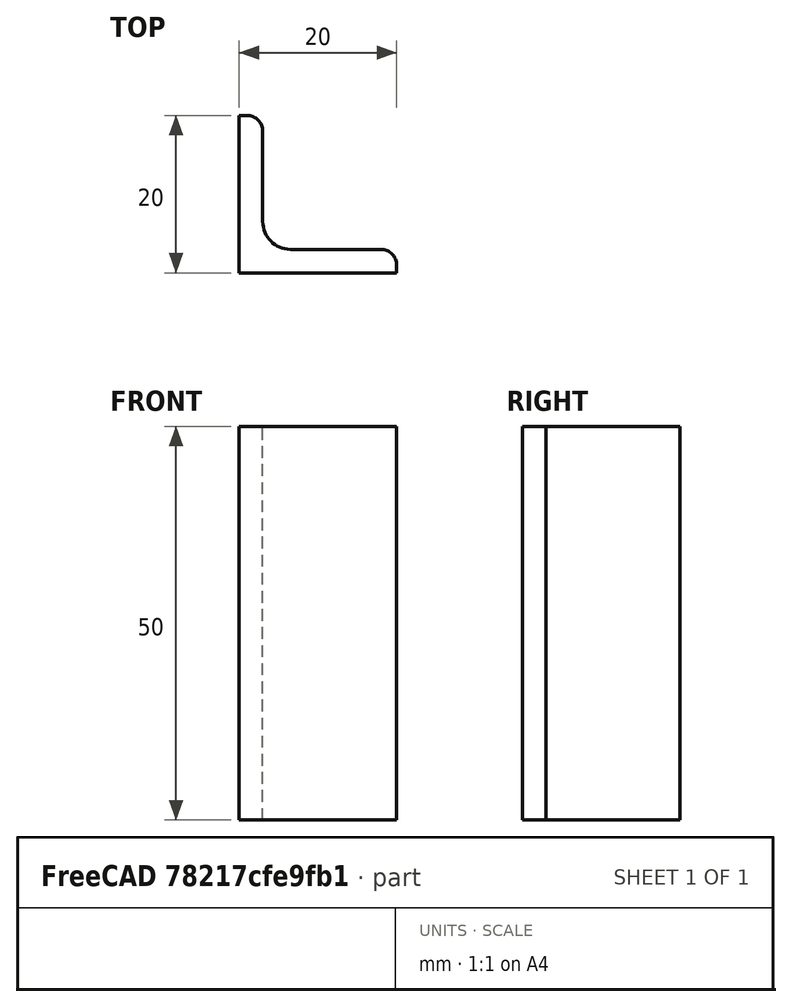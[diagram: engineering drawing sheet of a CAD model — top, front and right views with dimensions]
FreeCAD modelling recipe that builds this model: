
FCSTD DOCUMENT  (FreeCAD 0.15R4671 (Git))
Label: Angle Bar L20x20x3 EN10056 S235JR
License: All rights reserved
LicenseURL: http://en.wikipedia.org/wiki/All_rights_reserved
objects: Sketcher::SketchObject×1, Part::Extrusion×1
note: 2 computed .brp shape members not serialized (recipe doc carries the construction recipe); baked Part::Feature solids carry a one-line shape summary decoded from their .brp

FEATURE [Sketcher::SketchObject] Sketch
  sketch-geometry (9):
    g0: LineSegment StartX=0 StartY=0 StartZ=0 EndX=20 EndY=0 EndZ=0
    g1: LineSegment StartX=20 StartY=0 StartZ=0 EndX=20 EndY=1 EndZ=0
    g2: LineSegment StartX=18 StartY=3 StartZ=0 EndX=6.5 EndY=3 EndZ=0
    g3: LineSegment StartX=0 StartY=0 StartZ=0 EndX=0 EndY=20 EndZ=0
    g4: LineSegment StartX=0 StartY=20 StartZ=0 EndX=1 EndY=20 EndZ=0
    g5: LineSegment StartX=3 StartY=18 StartZ=0 EndX=3 EndY=6.5 EndZ=0
    g6: ArcOfCircle CenterX=6.5 CenterY=6.5 CenterZ=0 NormalX=0 NormalY=0 NormalZ=1 Radius=3.5 StartAngle=3.14159 EndAngle=4.71239
    g7: ArcOfCircle CenterX=1 CenterY=18 CenterZ=0 NormalX=0 NormalY=0 NormalZ=1 Radius=2 StartAngle=0 EndAngle=1.5708
    g8: ArcOfCircle CenterX=18 CenterY=1 CenterZ=0 NormalX=0 NormalY=0 NormalZ=1 Radius=2 StartAngle=0 EndAngle=1.5708
  constraints (23):
    c: Coincident(g0,g-1)
    c: Horizontal(g0)
    c: Coincident(g1,g0)
    c: Vertical(g1)
    c: Horizontal(g2)
    c: Coincident(g3,g-1)
    c: Vertical(g3)
    c: Coincident(g4,g3)
    c: Horizontal(g4)
    c: Vertical(g5)
    c: Tangent(g5,g6) = -1.5708
    c: Tangent(g2,g6) = 1.5708
    c: Tangent(g4,g7) = 1.5708
    c: Tangent(g5,g7) = 1.5708
    c: Tangent(g2,g8) = -1.5708
    c: Tangent(g1,g8) = -1.5708
    c: DistanceX(g0) = 20
    c: DistanceY(g3) = 20
    c: DistanceY(g0,g2) = 3
    c: DistanceX(g3,g5) = 3
    c: Radius(g6) = 3.5
    c: Radius(g8) = 2
    c: Radius(g7) = 2
FEATURE [Part::Extrusion] Extrude  label="Angle Bar L20x20x3 EN10056 S235JR"
  Base = -> Sketch
  Dir = (0,0,50)
  Solid = true
